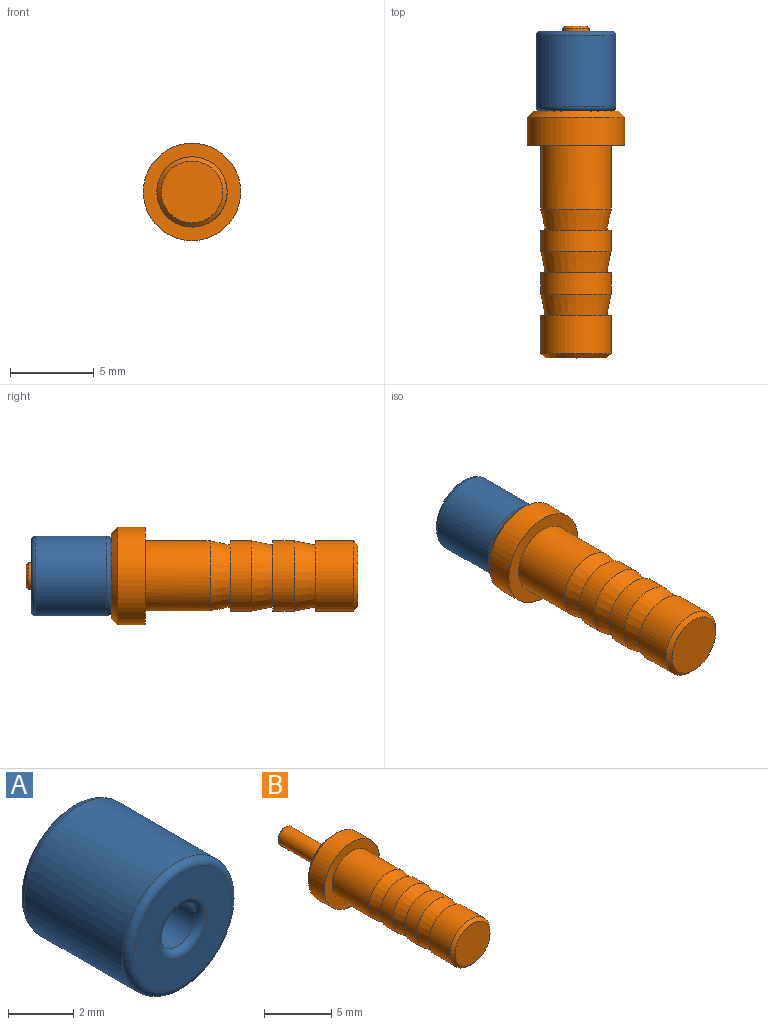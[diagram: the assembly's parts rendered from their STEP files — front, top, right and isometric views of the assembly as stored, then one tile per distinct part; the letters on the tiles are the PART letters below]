
ASSEMBLY  parts=2 mates=1
PART A: 8 faces, bbox 5.2x4.8x5.2 mm
  f0: cylinder r=0.79mm len=4.25mm, axis (0,-1,0), area 21.2mm2, adj f4,f7
  f1: cylinder r=2.38mm len=4.76mm, axis (0,-1,0), area 63.7mm2, adj f5,f6
  f2: plane 4.25x4.25mm, normal (0,1,0), area 10.8mm2, adj f5,f7
  f3: plane 4.25x4.25mm, normal (0,-1,0), area 10.8mm2, adj f4,f6
  f4: torus R=1.05mm, axis (0,1,0), area 2.2mm2, adj f0,f3
  f5: torus R=2.13mm, axis (0,1,0), area 5.7mm2, adj f1,f2
  f6: torus R=2.13mm, axis (0,1,0), area 5.7mm2, adj f1,f3
  f7: torus R=1.05mm, axis (0,1,0), area 2.2mm2, adj f0,f2
PART B: 20 faces, bbox 5.8x19.8x5.8 mm
  f0: cylinder r=2.91mm len=5.82mm, axis (0,1,0), area 30.2mm2, adj f1,f15
  f1: plane 5.82x5.82mm, normal (0,-1,0), area 12.8mm2, adj f0,f2
  f2: cylinder r=2.1mm len=4.19mm, axis (0,1,0), area 51mm2, adj f1,f3
  f3: cone r=1.84mm half-angle=11.9deg, axis (0,1,0), area 15.3mm2, adj f2,f4
  f4: plane 4.19x4.19mm, normal (0,1,0), area 3.1mm2, adj f3,f5
  f5: cylinder r=2.1mm len=4.19mm, axis (0,1,0), area 16.7mm2, adj f4,f7
  f6: plane 4.19x4.19mm, normal (0,1,0), area 3.1mm2, adj f7,f8
  f7: cone r=2.1mm half-angle=11.3deg, axis (0,1,0), area 16mm2, adj f5,f6
  f8: cylinder r=2.1mm len=4.19mm, axis (0,1,0), area 16.7mm2, adj f6,f9
  f9: cone r=2.1mm half-angle=11.3deg, axis (0,1,0), area 16mm2, adj f8,f10
  f10: plane 4.19x4.19mm, normal (0,1,0), area 3.1mm2, adj f9,f12
  f11: plane 3.68x3.68mm, normal (0,-1,0), area 10.7mm2, adj f13
  f12: cylinder r=2.1mm len=4.19mm, axis (0,1,0), area 30.1mm2, adj f10,f13
  f13: cone r=1.84mm half-angle=45deg, axis (0,1,0), area 4.4mm2, adj f11,f12
  f14: plane 5.05x5.05mm, normal (0,1,0), area 17.4mm2, adj f15,f18
  f15: cone r=2.91mm half-angle=45deg, axis (0,-1,0), area 9.2mm2, adj f0,f14
  f16: cylinder r=0.8mm len=4.83mm, axis (0,-1,0), area 24.3mm2, adj f18,f19
  f17: plane 1.35x1.35mm, normal (0,1,0), area 1.4mm2, adj f19
  f18: torus R=0.93mm, axis (0,-1,0), area 1.1mm2, adj f14,f16
  f19: cone r=0.67mm half-angle=45deg, axis (0,-1,0), area 0.8mm2, adj f16,f17
PLACE A rot(axis=(0,-1,0),7.8deg) t=(0,3.15,0)mm
PLACE B at identity fixed
MATE cylindrical A.f0 <-> B.f16  axis (0,-1,0) through (0,3.15,0)mm
